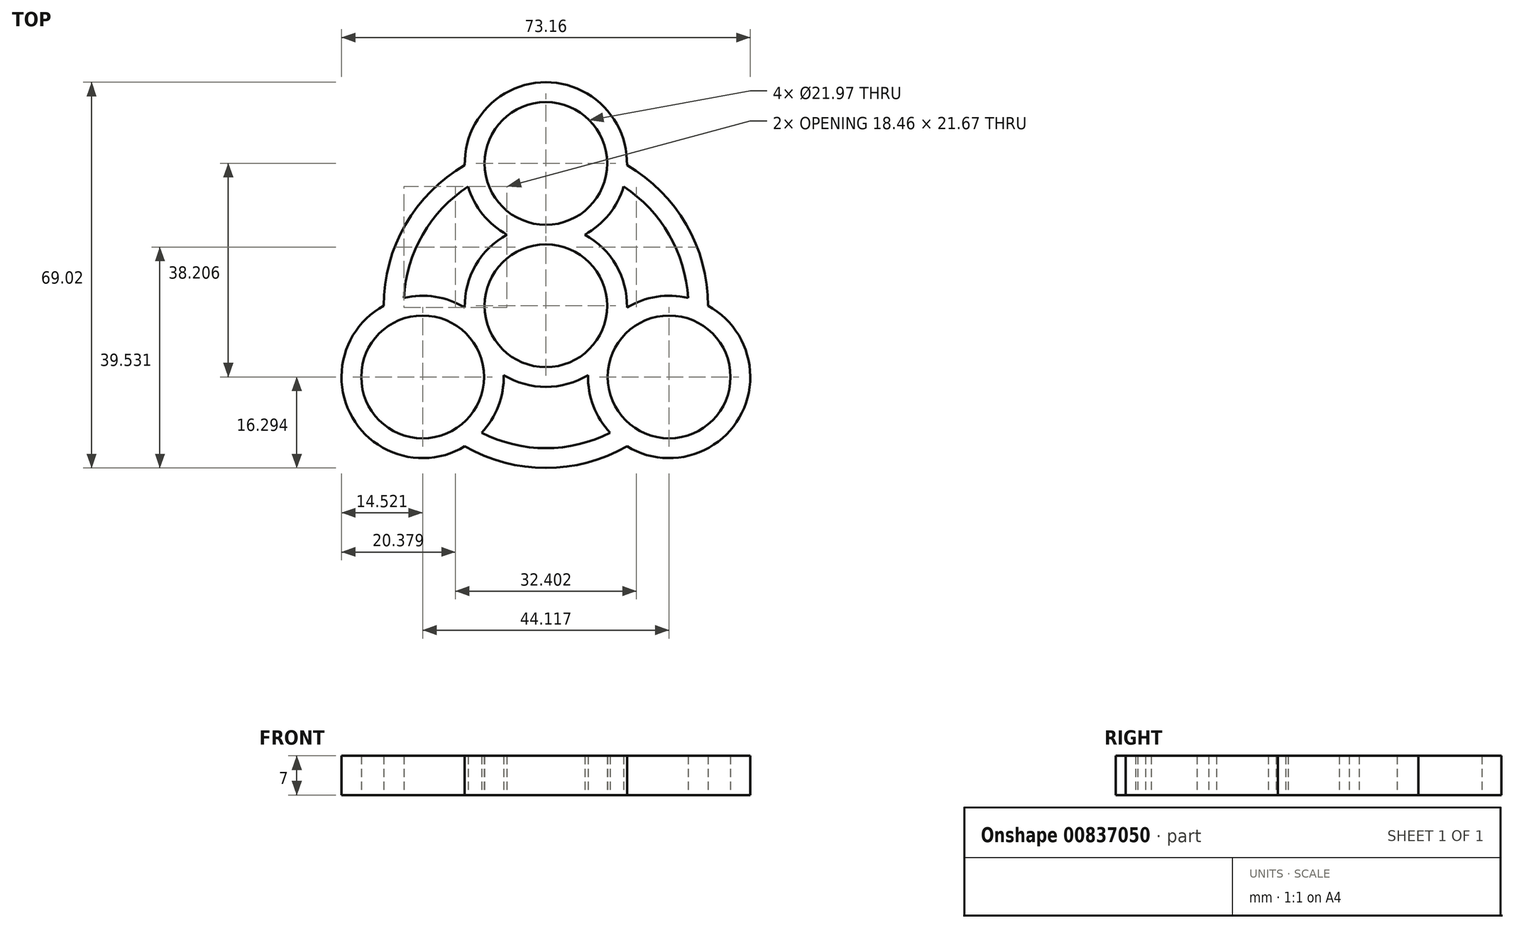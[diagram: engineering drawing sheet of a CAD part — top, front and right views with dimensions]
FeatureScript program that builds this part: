
annotation { "Feature Type Name" : "Feature", "Feature Type Description" : "" }
export const myFeature = defineFeature(function(context is Context, id is Id, definition is map)
    precondition{}
    {
        {
            var Q0;
            Q0=qCreatedBy(makeId("Top.planeOp"),FACE);
            var sketch = newSketch(context, id + "F0", { "sketchPlane" : qUnion([Q0])});
            skCircle(sketch, "E0", {"center": v(0, 0) * mm, "radius": 10.99 * mm});
            skArc(sketch, "E1", {"start": v(10.73, 23.1) * mm, "mid": v(0, 25.47) * mm, "end": v(-10.73, 23.1) * mm, "construction": true});
            skCircle(sketch, "E2", {"center": v(0, 25.47) * mm, "radius": 10.99 * mm});
            skCircle(sketch, "E3", {"center": v(-22.06, -12.74) * mm, "radius": 10.99 * mm});
            skCircle(sketch, "E4", {"center": v(22.06, -12.74) * mm, "radius": 10.99 * mm});
            skLineSegment(sketch, "E5", {"start": v(-22.06, -12.74) * mm, "end": v(7.54, -12.74) * mm, "construction": true});
            skLineSegment(sketch, "E6", {"start": v(0, 25.47) * mm, "end": v(-5.5, 15.96) * mm, "construction": true});
            skLineSegment(sketch, "E7", {"start": v(22.06, -12.74) * mm, "end": v(16.57, -3.22) * mm, "construction": true});
            skLineSegment(sketch, "E8.bottom", {"start": v(-57.15, 57.15) * mm, "end": v(57.15, 57.15) * mm, "construction": true});
            skLineSegment(sketch, "E8.top", {"start": v(-57.15, -57.15) * mm, "end": v(57.15, -57.15) * mm, "construction": true});
            skLineSegment(sketch, "E8.left", {"start": v(-57.15, 57.15) * mm, "end": v(-57.15, -57.15) * mm, "construction": true});
            skLineSegment(sketch, "E8.right", {"start": v(57.15, 57.15) * mm, "end": v(57.15, -57.15) * mm, "construction": true});
            skPoint(sketch, "E9", {"position": v(-57.15, 0) * mm});
            skPoint(sketch, "E10", {"position": v(0, 57.15) * mm});
            skArc(sketch, "E11", {"start": v(14.51, -25.14) * mm, "mid": v(34.63, -20) * mm, "end": v(29.03, 0) * mm});
            skArc(sketch, "E12", {"start": v(-13.92, 21.33) * mm, "mid": v(-11.3, 16.35) * mm, "end": v(-6.97, 12.74) * mm});
            skArc(sketch, "E13", {"start": v(-29.03, 0) * mm, "mid": v(-34.63, -20) * mm, "end": v(-14.51, -25.14) * mm});
            skArc(sketch, "E14", {"start": v(-10.73, 23.1) * mm, "mid": v(-21.1, 14.28) * mm, "end": v(-25.43, 1.38) * mm});
            skArc(sketch, "E15", {"start": v(25.43, 1.38) * mm, "mid": v(22.06, 12.74) * mm, "end": v(13.92, 21.33) * mm});
            skArc(sketch, "E16", {"start": v(-11.52, -22.72) * mm, "mid": v(0, -25.47) * mm, "end": v(11.52, -22.72) * mm});
            skArc(sketch, "E17", {"start": v(-14.51, 25.14) * mm, "mid": v(-25.14, 14.51) * mm, "end": v(-29.03, 0) * mm});
            skArc(sketch, "E18", {"start": v(29.03, 0) * mm, "mid": v(25.14, 14.51) * mm, "end": v(14.51, 25.14) * mm});
            skArc(sketch, "E19", {"start": v(-14.51, -25.14) * mm, "mid": v(0, -29.03) * mm, "end": v(14.51, -25.14) * mm});
            skArc(sketch, "E20", {"start": v(-12.88, -6.7) * mm, "mid": v(-12.57, -7.26) * mm, "end": v(-12.25, -7.8) * mm});
            skLineSegment(sketch, "E21.trimOffspring", {"start": v(-14.51, 0.33) * mm, "end": v(-22.06, -12.74) * mm, "construction": true});
            skArc(sketch, "E22.trimOffspring", {"start": v(-11.52, -22.72) * mm, "mid": v(-8.51, -17.95) * mm, "end": v(-7.55, -12.4) * mm});
            skArc(sketch, "E23.trimOffspring", {"start": v(-9.18, -6.03) * mm, "mid": v(-9.49, -5.48) * mm, "end": v(-9.81, -4.94) * mm});
            skArc(sketch, "E24.trimOffspring", {"start": v(-7.55, -12.4) * mm, "mid": v(0, -14.52) * mm, "end": v(7.55, -12.4) * mm});
            skArc(sketch, "E25.trimOffspring", {"start": v(-14.51, -0.33) * mm, "mid": v(-19.8, 1.6) * mm, "end": v(-25.43, 1.38) * mm});
            skArc(sketch, "E26.trimOffspring", {"start": v(25.43, 1.38) * mm, "mid": v(19.8, 1.6) * mm, "end": v(14.51, -0.33) * mm});
            skLineSegment(sketch, "E27.trimOffspring", {"start": v(11.07, -12.74) * mm, "end": v(22.06, -12.74) * mm, "construction": true});
            skLineSegment(sketch, "E28.trimOffspring", {"start": v(14.8, -0.16) * mm, "end": v(7.26, 12.9) * mm, "construction": true});
            skArc(sketch, "E29.trimOffspring", {"start": v(14.51, -0.33) * mm, "mid": v(12.57, 7.26) * mm, "end": v(6.97, 12.74) * mm});
            skArc(sketch, "E30.trimOffspring", {"start": v(12.25, -7.8) * mm, "mid": v(12.57, -7.26) * mm, "end": v(12.88, -6.7) * mm});
            skArc(sketch, "E31.trimOffspring", {"start": v(9.81, -4.94) * mm, "mid": v(9.49, -5.48) * mm, "end": v(9.18, -6.03) * mm});
            skArc(sketch, "E32.trimOffspring", {"start": v(7.55, -12.4) * mm, "mid": v(8.51, -17.95) * mm, "end": v(11.52, -22.72) * mm});
            skArc(sketch, "E33.trimOffspring", {"start": v(14.51, 25.14) * mm, "mid": v(0, 39.99) * mm, "end": v(-14.51, 25.14) * mm});
            skLineSegment(sketch, "E34.trimOffspring", {"start": v(5.5, 15.96) * mm, "end": v(0, 25.47) * mm, "construction": true});
            skLineSegment(sketch, "E35.trimOffspring", {"start": v(-7.26, 12.9) * mm, "end": v(-7.55, 12.4) * mm, "construction": true});
            skArc(sketch, "E36.trimOffspring", {"start": v(-6.97, 12.74) * mm, "mid": v(-12.57, 7.26) * mm, "end": v(-14.51, -0.33) * mm});
            skArc(sketch, "E37.trimOffspring", {"start": v(0.63, 14.5) * mm, "mid": v(0, 14.52) * mm, "end": v(-0.63, 14.5) * mm});
            skArc(sketch, "E38.trimOffspring", {"start": v(6.97, 12.74) * mm, "mid": v(11.3, 16.35) * mm, "end": v(13.92, 21.33) * mm});
            skArc(sketch, "E39.trimOffspring", {"start": v(-0.63, 10.97) * mm, "mid": v(0, 10.95) * mm, "end": v(0.63, 10.97) * mm});
            skArc(sketch, "E40.trimOffspring", {"start": v(-13.92, 21.33) * mm, "mid": v(0, -25.47) * mm, "end": v(13.92, 21.33) * mm, "construction": true});
            skSolve(sketch);
        }
        {
            var Q0;
            Q0=qSketchRegion(id+"F0",true);
            extrude(context, id + "F1", {"entities" : qUnion([Q0]), "depth" : 7 * mm, "offsetDistance" : 25.4 * mm});
        }
    });
